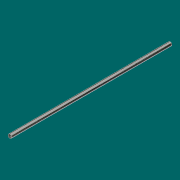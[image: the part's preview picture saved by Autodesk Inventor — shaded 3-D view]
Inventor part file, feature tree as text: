
AUTODESK INVENTOR PART (.ipt)
format: ipt  version: 2017 (Build 210142000, 142)  size: 68,096 bytes
history: native  units: in
note: dims shown in document units (in); Inventor stores cm internally (conversion verified against a paired STEP export)
features: extrude x1, sketch x1
ambient origin geometry x8: Origin, YZ Plane, XZ Plane, XY Plane, X Axis, Y Axis, Z Axis, Center Point
bodies: Solid1 (feature_tree)
feature tree (2):
  extrude  "Extrusion1"  Depth=96.0in TaperAngle=0.0deg
  sketch  "Sketch1"  dims[d0=2.25in d1=96.0in d2=0.0in]
